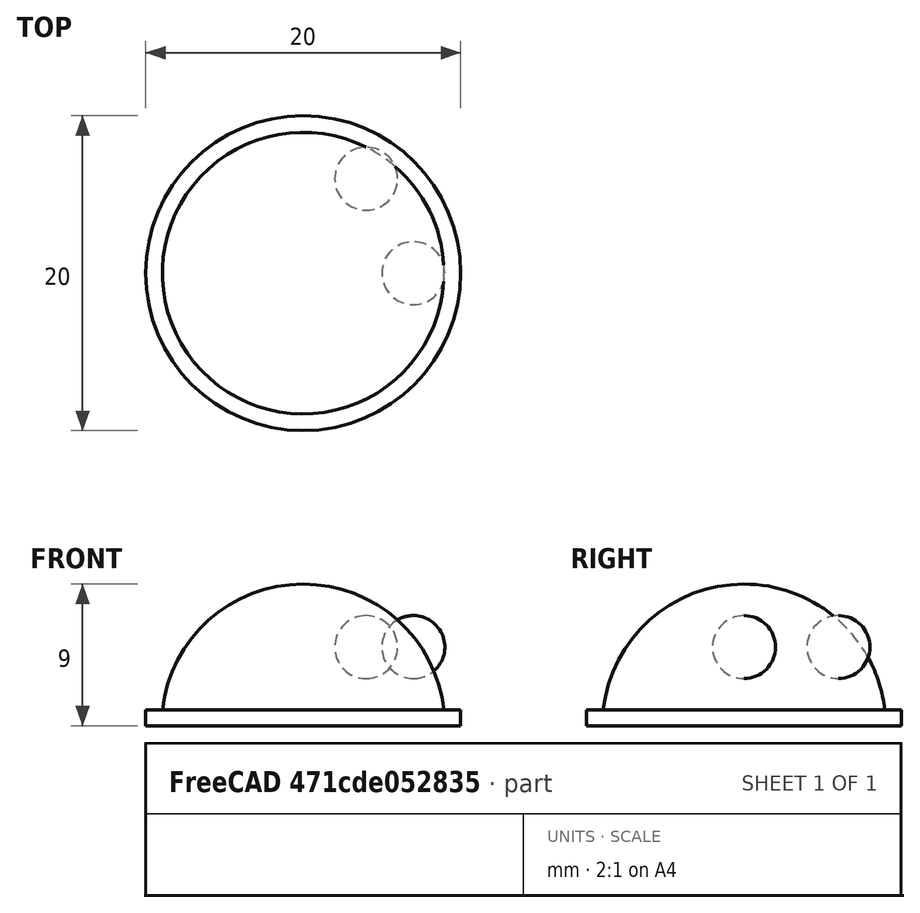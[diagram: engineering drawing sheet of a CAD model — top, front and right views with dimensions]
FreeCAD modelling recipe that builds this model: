
FCSTD DOCUMENT  (FreeCAD 0.21R33694 (Git))
Label: OJT1_T13R01_robot
License: All rights reserved
LicenseURL: http://en.wikipedia.org/wiki/All_rights_reserved
objects: Part::Sphere×3, Part::Cylinder×1, Part::MultiFuse×1
note: 5 computed .brp shape members not serialized (recipe doc carries the construction recipe); baked Part::Feature solids carry a one-line shape summary decoded from their .brp

FEATURE [Part::Cylinder] Cylinder
  Angle = 360
  AttacherType = Attacher::AttachEngine3D
  FirstAngle = 0
  Height = 1
  Radius = 10
  SecondAngle = 0
FEATURE [Part::Sphere] Sphere
  Angle1 = 0
  Angle2 = 90
  Angle3 = 360
  AttacherType = Attacher::AttachEngine3D
  Radius = 9
FEATURE [Part::MultiFuse] Fusion
  Refine = true
  Shapes = -> [Sphere,Cylinder]
FEATURE [Part::Sphere] Sphere001
  Angle1 = -90
  Angle2 = 90
  Angle3 = 360
  AttacherType = Attacher::AttachEngine3D
  Placement = pos=(7,0,5) rot=(0,0,1;0rad)
  Radius = 2
FEATURE [Part::Sphere] Sphere002
  Angle1 = -90
  Angle2 = 90
  Angle3 = 360
  AttacherType = Attacher::AttachEngine3D
  Placement = pos=(4,6,5) rot=(0,0,1;0rad)
  Radius = 2
